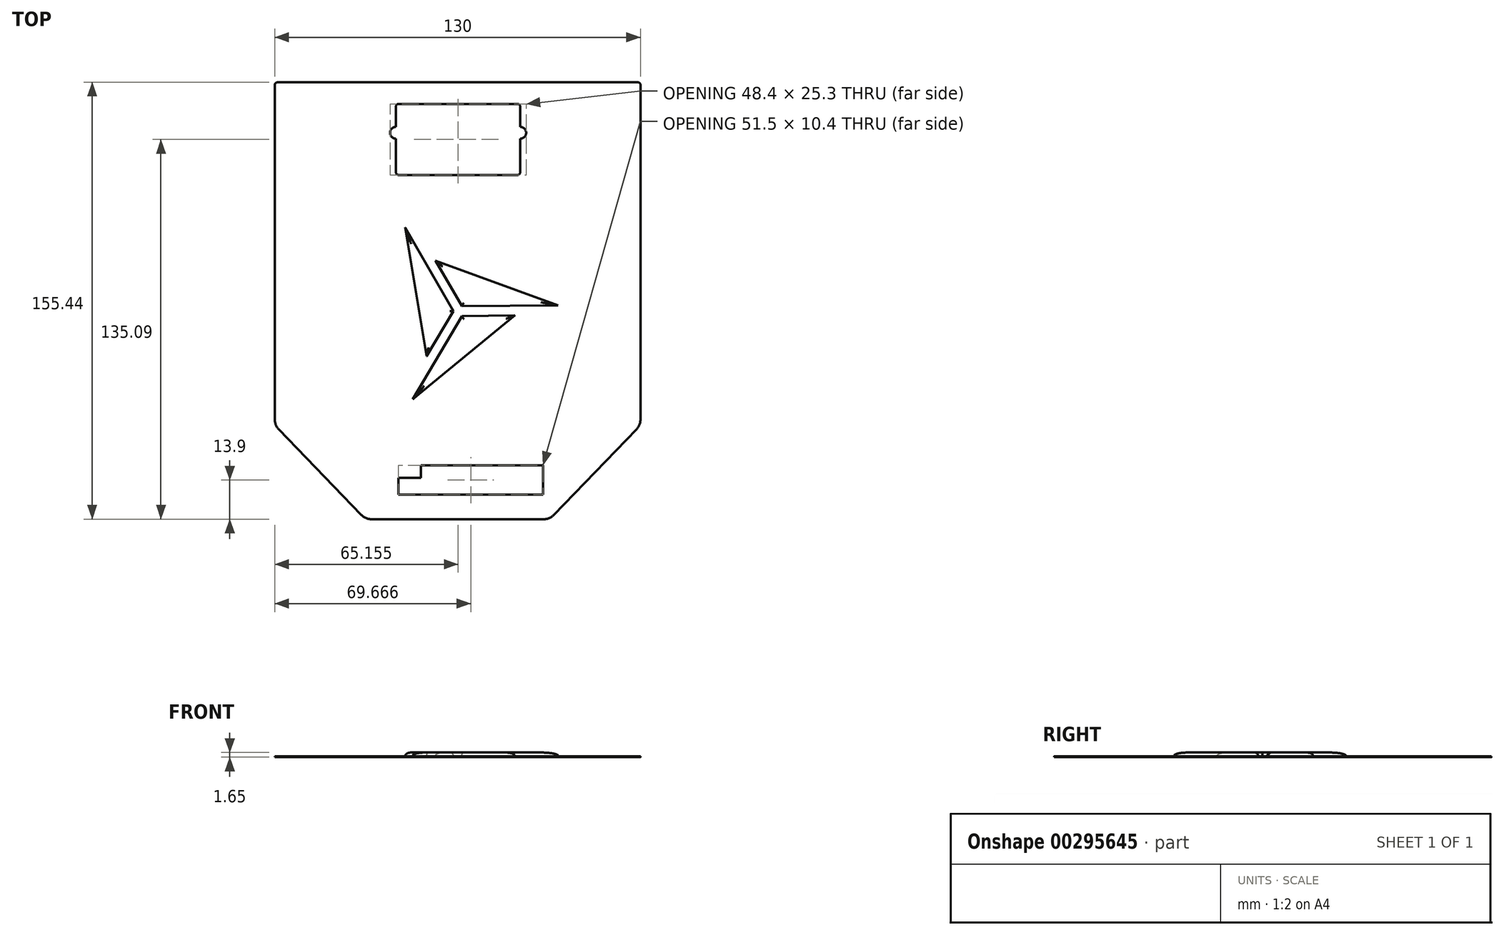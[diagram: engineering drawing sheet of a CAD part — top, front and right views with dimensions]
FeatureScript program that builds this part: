
annotation { "Feature Type Name" : "Feature", "Feature Type Description" : "" }
export const myFeature = defineFeature(function(context is Context, id is Id, definition is map)
    precondition{}
    {
        {
            var Q0;
            Q0=qCreatedBy(makeId("Top.planeOp"),FACE);
            var sketch = newSketch(context, id + "F0", { "sketchPlane" : qUnion([Q0])});
            skLineSegment(sketch, "E0", {"start": v(47.84, 85.95) * mm, "end": v(47.84, -33.05) * mm});
            skLineSegment(sketch, "E1", {"start": v(46.44, -36.52) * mm, "end": v(17.07, -66.96) * mm});
            skLineSegment(sketch, "E2", {"start": v(13.47, -68.49) * mm, "end": v(-47.79, -68.49) * mm});
            skLineSegment(sketch, "E3", {"start": v(-80.76, -36.52) * mm, "end": v(-51.39, -66.96) * mm});
            skLineSegment(sketch, "E4", {"start": v(-82.16, -33.05) * mm, "end": v(-82.16, 85.95) * mm});
            skLineSegment(sketch, "E5", {"start": v(-81.16, 86.95) * mm, "end": v(46.84, 86.95) * mm});
            skArc(sketch, "E6", {"start": v(47.84, 85.95) * mm, "mid": v(47.55, 86.65) * mm, "end": v(46.84, 86.95) * mm});
            skArc(sketch, "E7", {"start": v(46.44, -36.52) * mm, "mid": v(47.48, -34.92) * mm, "end": v(47.84, -33.05) * mm});
            skArc(sketch, "E8", {"start": v(13.47, -68.49) * mm, "mid": v(15.43, -68.1) * mm, "end": v(17.07, -66.96) * mm});
            skArc(sketch, "E9", {"start": v(-51.39, -66.96) * mm, "mid": v(-49.74, -68.1) * mm, "end": v(-47.79, -68.49) * mm});
            skArc(sketch, "E10", {"start": v(-82.16, -33.05) * mm, "mid": v(-81.8, -34.92) * mm, "end": v(-80.76, -36.52) * mm});
            skArc(sketch, "E11", {"start": v(-81.16, 86.95) * mm, "mid": v(-81.87, 86.65) * mm, "end": v(-82.16, 85.95) * mm});
            skLineSegment(sketch, "E12", {"start": v(-38.1, 79.25) * mm, "end": v(4.1, 79.25) * mm});
            skLineSegment(sketch, "E13", {"start": v(5.1, 78.25) * mm, "end": v(5.1, 71.05) * mm});
            skLineSegment(sketch, "E14", {"start": v(5.1, 66.85) * mm, "end": v(5.1, 54.95) * mm});
            skLineSegment(sketch, "E15", {"start": v(4.1, 53.95) * mm, "end": v(-38.1, 53.95) * mm});
            skLineSegment(sketch, "E16", {"start": v(-39.1, 54.95) * mm, "end": v(-39.1, 66.85) * mm});
            skLineSegment(sketch, "E17", {"start": v(-39.1, 71.05) * mm, "end": v(-39.1, 78.25) * mm});
            skArc(sketch, "E18", {"start": v(-38.1, 79.25) * mm, "mid": v(-38.81, 78.96) * mm, "end": v(-39.1, 78.25) * mm});
            skArc(sketch, "E19", {"start": v(5.1, 78.25) * mm, "mid": v(4.8, 78.96) * mm, "end": v(4.1, 79.25) * mm});
            skArc(sketch, "E20", {"start": v(5.1, 66.85) * mm, "mid": v(7.2, 68.95) * mm, "end": v(5.1, 71.05) * mm});
            skArc(sketch, "E21", {"start": v(4.1, 53.95) * mm, "mid": v(4.8, 54.24) * mm, "end": v(5.1, 54.95) * mm});
            skArc(sketch, "E22", {"start": v(-39.1, 54.95) * mm, "mid": v(-38.81, 54.24) * mm, "end": v(-38.1, 53.95) * mm});
            skArc(sketch, "E23", {"start": v(-39.1, 71.05) * mm, "mid": v(-41.2, 68.95) * mm, "end": v(-39.1, 66.85) * mm});
            skSolve(sketch);
        }
        {
            var Q0;
            Q0 = qSketchRegion(id + "F0", true);
            extrude(context, id + "F1", {"entities" : qUnion([Q0]), "depth" : 0.35 * mm, "offsetDistance" : 25 * mm});
        }
        {
            var Q0;
            Q0=makeQuery(id+"F1.opExtrude","CAP_FACE",FACE,{"disambiguationData":[OSD([sQuery(id+"F0.wireOp",EDGE,"E0"),sQuery(id+"F0.wireOp",EDGE,"E1"),sQuery(id+"F0.wireOp",EDGE,"E2"),sQuery(id+"F0.wireOp",EDGE,"E3"),sQuery(id+"F0.wireOp",EDGE,"E4"),sQuery(id+"F0.wireOp",EDGE,"E5"),sQuery(id+"F0.wireOp",EDGE,"E6"),sQuery(id+"F0.wireOp",EDGE,"E7"),sQuery(id+"F0.wireOp",EDGE,"E8"),sQuery(id+"F0.wireOp",EDGE,"E9"),sQuery(id+"F0.wireOp",EDGE,"E10"),sQuery(id+"F0.wireOp",EDGE,"E11"),sQuery(id+"F0.wireOp",EDGE,"E12"),sQuery(id+"F0.wireOp",EDGE,"E13"),sQuery(id+"F0.wireOp",EDGE,"E14"),sQuery(id+"F0.wireOp",EDGE,"E15"),sQuery(id+"F0.wireOp",EDGE,"E16"),sQuery(id+"F0.wireOp",EDGE,"E17"),sQuery(id+"F0.wireOp",EDGE,"E18"),sQuery(id+"F0.wireOp",EDGE,"E19"),sQuery(id+"F0.wireOp",EDGE,"E20"),sQuery(id+"F0.wireOp",EDGE,"E21"),sQuery(id+"F0.wireOp",EDGE,"E22"),sQuery(id+"F0.wireOp",EDGE,"E23"),sQuery(id+"F0.wireOp",EDGE,"c2f3efe0-b904-4345-a17c-e8e102eab4bb"),sQuery(id+"F0.wireOp",EDGE,"bc6f52a4-2d46-4615-8a24-8c402133adb3"),sQuery(id+"F0.wireOp",EDGE,"871bb449-fccb-480d-9c76-3cdbeeecd939"),sQuery(id+"F0.wireOp",EDGE,"b22824b2-7bac-4383-aba4-ed6bdb453358")])],"isStart":false});
            var sketch = newSketch(context, id + "F2", { "sketchPlane" : qUnion([Q0])});
            skLineSegment(sketch, "E24.bottom", {"start": v(-30.24, -49.39) * mm, "end": v(13.26, -49.39) * mm});
            skLineSegment(sketch, "E24.top", {"start": v(-30.24, -59.79) * mm, "end": v(13.26, -59.79) * mm});
            skLineSegment(sketch, "E25", {"start": v(13.26, -49.39) * mm, "end": v(13.26, -59.79) * mm});
            skLineSegment(sketch, "E26.bottom", {"start": v(-30.24, -59.79) * mm, "end": v(-38.24, -59.79) * mm});
            skLineSegment(sketch, "E26.top", {"start": v(-30.24, -53.79) * mm, "end": v(-38.24, -53.79) * mm});
            skLineSegment(sketch, "E26.right", {"start": v(-38.24, -59.79) * mm, "end": v(-38.24, -53.79) * mm});
            skLineSegment(sketch, "E27", {"start": v(-30.24, -53.79) * mm, "end": v(-30.24, -49.39) * mm});
            skSolve(sketch);
        }
        {
            var Q0;
            Q0 = qSketchRegion(id + "F2", true);
            extrude(context, id + "F3", {"entities" : qUnion([Q0]), "operationType" : NewBodyOperationType.REMOVE, "oppositeDirection" : true, "depth" : 2 * mm, "offsetDistance" : 25 * mm});
        }
        {
            var Q0;
            Q0=makeQuery(id+"F1.opExtrude","CAP_FACE",FACE,{"disambiguationData":[OSD([sQuery(id+"F0.wireOp",EDGE,"E0"),sQuery(id+"F0.wireOp",EDGE,"E1"),sQuery(id+"F0.wireOp",EDGE,"E2"),sQuery(id+"F0.wireOp",EDGE,"E3"),sQuery(id+"F0.wireOp",EDGE,"E4"),sQuery(id+"F0.wireOp",EDGE,"E5"),sQuery(id+"F0.wireOp",EDGE,"E6"),sQuery(id+"F0.wireOp",EDGE,"E7"),sQuery(id+"F0.wireOp",EDGE,"E8"),sQuery(id+"F0.wireOp",EDGE,"E9"),sQuery(id+"F0.wireOp",EDGE,"E10"),sQuery(id+"F0.wireOp",EDGE,"E11"),sQuery(id+"F0.wireOp",EDGE,"E12"),sQuery(id+"F0.wireOp",EDGE,"E13"),sQuery(id+"F0.wireOp",EDGE,"E14"),sQuery(id+"F0.wireOp",EDGE,"E15"),sQuery(id+"F0.wireOp",EDGE,"E16"),sQuery(id+"F0.wireOp",EDGE,"E17"),sQuery(id+"F0.wireOp",EDGE,"E18"),sQuery(id+"F0.wireOp",EDGE,"E19"),sQuery(id+"F0.wireOp",EDGE,"E20"),sQuery(id+"F0.wireOp",EDGE,"E21"),sQuery(id+"F0.wireOp",EDGE,"E22"),sQuery(id+"F0.wireOp",EDGE,"E23")])],"isStart":false});
            var sketch = newSketch(context, id + "F4", { "sketchPlane" : qUnion([Q0])});
            skLineSegment(sketch, "E28.0", {"start": v(-28.15, -10.53) * mm, "end": v(-35.8, 35.19) * mm});
            skLineSegment(sketch, "E28.1", {"start": v(-18.68, 5.55) * mm, "end": v(-28.15, -10.53) * mm});
            skLineSegment(sketch, "E28.2", {"start": v(-35.8, 35.19) * mm, "end": v(-18.68, 5.55) * mm});
            skLineSegment(sketch, "E29.0", {"start": v(-24.98, 23.47) * mm, "end": v(18.57, 7.6) * mm});
            skLineSegment(sketch, "E29.1", {"start": v(-15.65, 7.3) * mm, "end": v(-24.98, 23.47) * mm});
            skLineSegment(sketch, "E29.2", {"start": v(18.57, 7.6) * mm, "end": v(-15.65, 7.3) * mm});
            skLineSegment(sketch, "E30.0", {"start": v(3.14, 3.97) * mm, "end": v(-33.13, -25.88) * mm});
            skLineSegment(sketch, "E30.1", {"start": v(-15.65, 3.8) * mm, "end": v(3.14, 3.97) * mm});
            skLineSegment(sketch, "E30.2", {"start": v(-33.13, -25.88) * mm, "end": v(-15.65, 3.8) * mm});
            skLineSegment(sketch, "E31.0", {"start": v(-18.68, 5.55) * mm, "end": v(-15.65, 7.3) * mm, "construction": true});
            skLineSegment(sketch, "E31.1", {"start": v(-29.44, 18.13) * mm, "end": v(-29.44, 18.13) * mm});
            skSolve(sketch);
        }
        {
            var Q0;
            Q0 = qSketchRegion(id + "F4", true);
            extrude(context, id + "F5", {"entities" : qUnion([Q0]), "operationType" : NewBodyOperationType.ADD, "depth" : 1.3 * mm, "offsetDistance" : 25 * mm});
        }
        {
            var Q0;
            Q0=makeQuery(id+"F5.opExtrude","CAP_FACE",FACE,{"disambiguationData":[OSD([sQuery(id+"F4.wireOp",EDGE,"E30.0"),sQuery(id+"F4.wireOp",EDGE,"E30.1"),sQuery(id+"F4.wireOp",EDGE,"E30.2")])],"isStart":false});
            var Q1;
            Q1=makeQuery(id+"F5.opExtrude","CAP_FACE",FACE,{"disambiguationData":[OSD([sQuery(id+"F4.wireOp",EDGE,"E28.0"),sQuery(id+"F4.wireOp",EDGE,"E28.1"),sQuery(id+"F4.wireOp",EDGE,"E28.2")])],"isStart":false});
            var Q2;
            Q2=makeQuery(id+"F5.opExtrude","CAP_FACE",FACE,{"disambiguationData":[OSD([sQuery(id+"F4.wireOp",EDGE,"E29.0"),sQuery(id+"F4.wireOp",EDGE,"E29.1"),sQuery(id+"F4.wireOp",EDGE,"E29.2")])],"isStart":false});
            fillet(context, id + "F6", {"entities" : qUnion([Q0, Q1, Q2]), "radius" : 1.1 * mm, "tangentPropagation" : true, "allowEdgeOverflow" : false});
        }
    });
